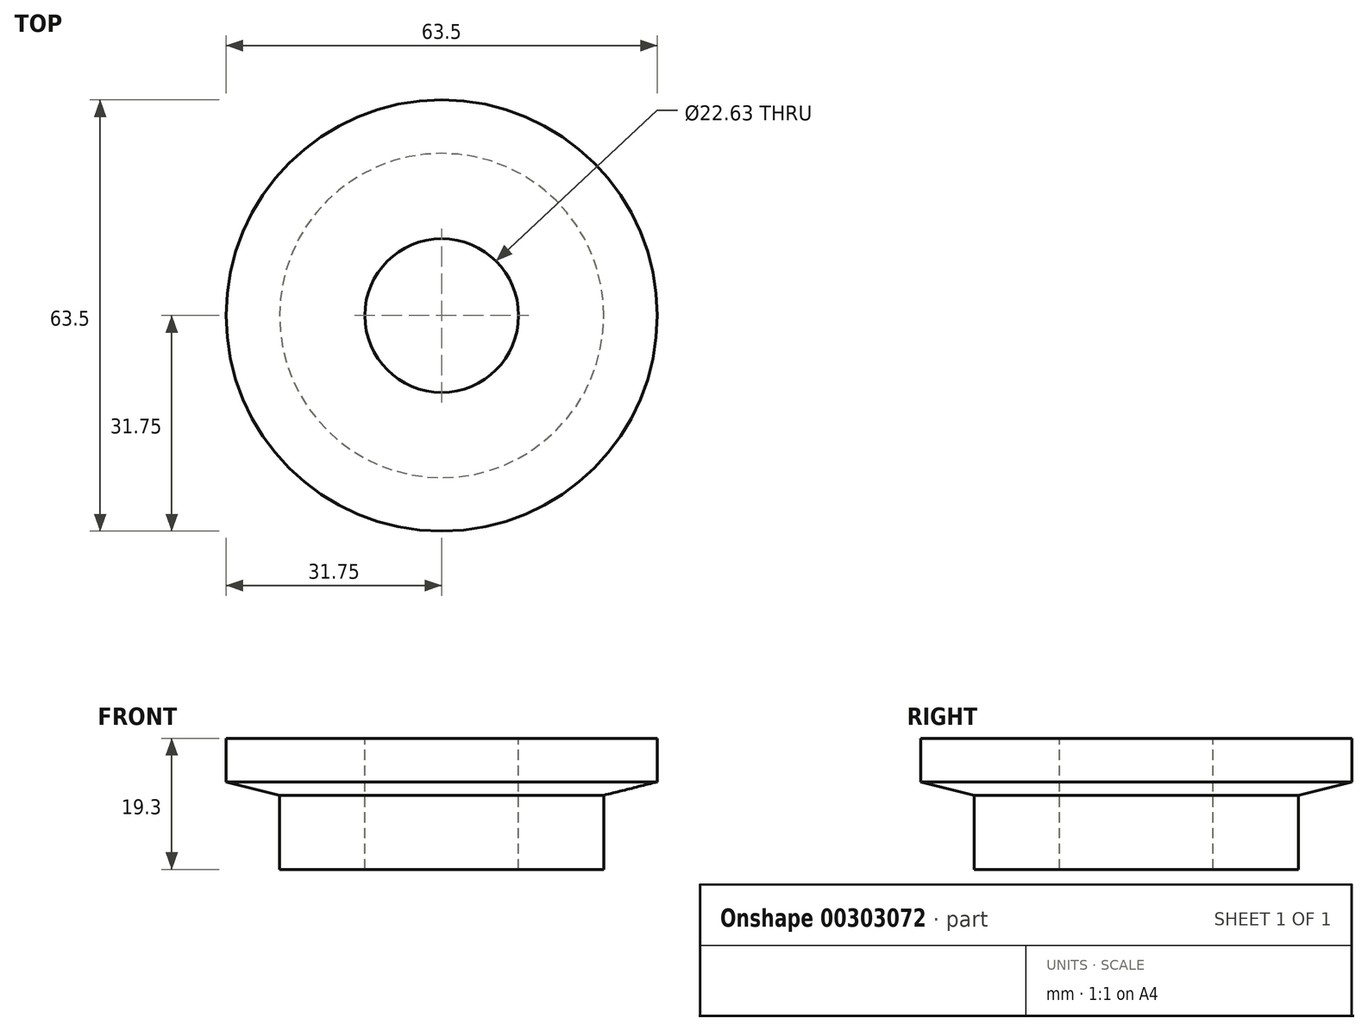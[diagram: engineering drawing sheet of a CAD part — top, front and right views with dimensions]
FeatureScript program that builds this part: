
annotation { "Feature Type Name" : "Feature", "Feature Type Description" : "" }
export const myFeature = defineFeature(function(context is Context, id is Id, definition is map)
    precondition{}
    {
        {
            var Q0;
            Q0=qCreatedBy(makeId("Front.planeOp"),FACE);
            var sketch = newSketch(context, id + "F0", { "sketchPlane" : qUnion([Q0])});
            skLineSegment(sketch, "E0", {"start": v(0, 15.77) * mm, "end": v(0, -16.78) * mm, "construction": true});
            skLineSegment(sketch, "E1", {"start": v(0, 9.65) * mm, "end": v(-31.75, 9.65) * mm});
            skLineSegment(sketch, "E2", {"start": v(-31.75, 9.65) * mm, "end": v(-31.75, 3.23) * mm});
            skLineSegment(sketch, "E3", {"start": v(-31.75, 3.23) * mm, "end": v(-23.88, 1.27) * mm});
            skLineSegment(sketch, "E4", {"start": v(-23.88, 1.27) * mm, "end": v(-23.88, -9.65) * mm});
            skLineSegment(sketch, "E5", {"start": v(-23.88, -9.65) * mm, "end": v(0, -9.65) * mm});
            skLineSegment(sketch, "E6", {"start": v(-11.32, 9.65) * mm, "end": v(-11.32, -9.65) * mm});
            skLineSegment(sketch, "E7.MirrorCS", {"start": v(31.75, 9.65) * mm, "end": v(31.75, 3.23) * mm});
            skLineSegment(sketch, "E8.MirrorCS", {"start": v(11.32, 9.65) * mm, "end": v(11.32, -9.65) * mm});
            skLineSegment(sketch, "E9.MirrorCS", {"start": v(23.88, -9.65) * mm, "end": v(0, -9.65) * mm});
            skLineSegment(sketch, "E10.MirrorCS", {"start": v(23.88, 1.27) * mm, "end": v(23.88, -9.65) * mm});
            skLineSegment(sketch, "E11.MirrorCS", {"start": v(0, 9.65) * mm, "end": v(31.75, 9.65) * mm});
            skLineSegment(sketch, "E12.MirrorCS", {"start": v(31.75, 3.23) * mm, "end": v(23.88, 1.27) * mm});
            skSolve(sketch);
        }
        {
            var Q0;
            {var subQ1=sQuery(id+"F0.wireOp",EDGE,"E2");Q0=makeQuery(id+"F0.imprint","IMPRINT",FACE,{"disambiguationData":[TD([[makeQuery(id+"F0.imprint","IMPRINT",EDGE,{"derivedFrom":subQ1}),1.0]])]});}
            var Q1;
            Q1=sQuery(id+"F0.wireOp",EDGE,"E0");
            revolve(context, id + "F1", {"entities" : qUnion([Q0]), "axis" : qUnion([Q1]), "revolveType" : RevolveType.FULL});
        }
    });
